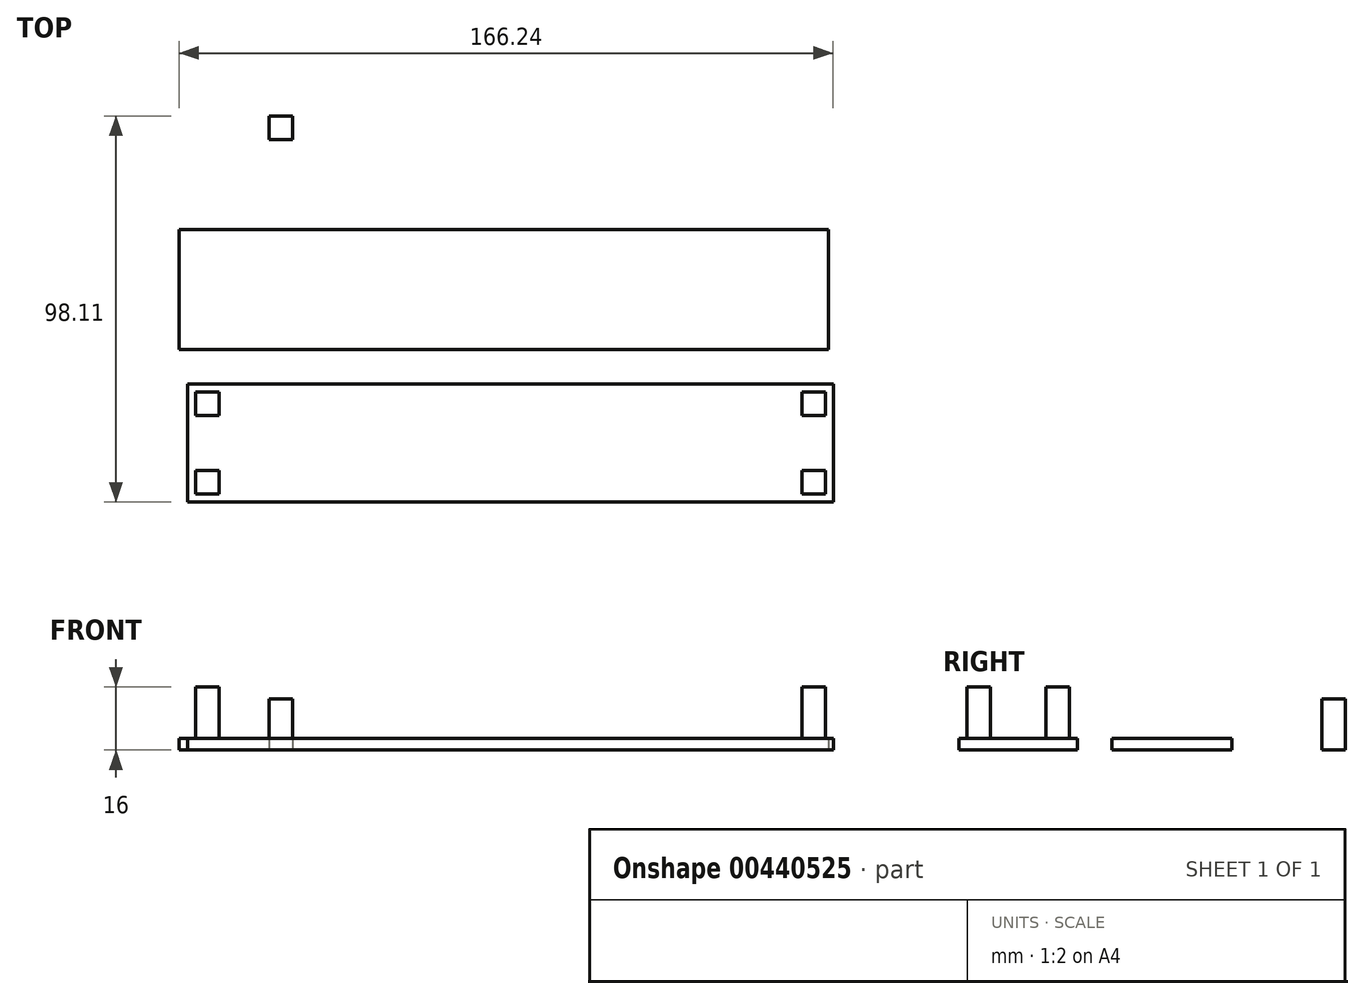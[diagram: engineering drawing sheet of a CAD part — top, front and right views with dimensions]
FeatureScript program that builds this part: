
annotation { "Feature Type Name" : "Feature", "Feature Type Description" : "" }
export const myFeature = defineFeature(function(context is Context, id is Id, definition is map)
    precondition{}
    {
        {
            var Q0;
            Q0=qCreatedBy(makeId("Top.planeOp"),FACE);
            var sketch = newSketch(context, id + "F0", { "sketchPlane" : qUnion([Q0])});
            skLineSegment(sketch, "E0.bottom", {"start": v(-85.08, 12.28) * mm, "end": v(79.92, 12.28) * mm});
            skLineSegment(sketch, "E0.top", {"start": v(-85.08, -18.22) * mm, "end": v(79.92, -18.22) * mm});
            skLineSegment(sketch, "E0.left", {"start": v(-85.08, 12.28) * mm, "end": v(-85.08, -18.22) * mm});
            skLineSegment(sketch, "E0.right", {"start": v(79.92, 12.28) * mm, "end": v(79.92, -18.22) * mm});
            skSolve(sketch);
        }
        {
            var Q0;
            Q0=qCreatedBy(makeId("Top.planeOp"),FACE);
            var sketch = newSketch(context, id + "F1", { "sketchPlane" : qUnion([Q0])});
            skLineSegment(sketch, "E1.bottom", {"start": v(-62.2, 41.13) * mm, "end": v(-56.2, 41.13) * mm});
            skLineSegment(sketch, "E1.top", {"start": v(-62.2, 35.13) * mm, "end": v(-56.2, 35.13) * mm});
            skLineSegment(sketch, "E1.left", {"start": v(-62.2, 41.13) * mm, "end": v(-62.2, 35.13) * mm});
            skLineSegment(sketch, "E1.right", {"start": v(-56.2, 41.13) * mm, "end": v(-56.2, 35.13) * mm});
            skSolve(sketch);
        }
        {
            var Q0;
            Q0=makeQuery(id+"F0.imprint","IMPRINT",FACE,{"disambiguationData":[TD([[makeQuery(id+"F0.imprint","IMPRINT",EDGE,{"derivedFrom":sQuery(id+"F0.wireOp",EDGE,"E0.bottom")}),-1.0]])]});
            extrude(context, id + "F2", {"entities" : qUnion([Q0]), "depth" : 3 * mm, "offsetDistance" : 25 * mm});
        }
        {
            var Q0;
            Q0=makeQuery(id+"F1.imprint","IMPRINT",FACE,{"disambiguationData":[TD([[makeQuery(id+"F1.imprint","IMPRINT",EDGE,{"derivedFrom":sQuery(id+"F1.wireOp",EDGE,"E1.bottom")}),-1.0]])]});
            extrude(context, id + "F3", {"entities" : qUnion([Q0]), "depth" : 13 * mm, "offsetDistance" : 25 * mm});
        }
        {
            var Q0;
            Q0=qCreatedBy(makeId("Top.planeOp"),FACE);
            var sketch = newSketch(context, id + "F4", { "sketchPlane" : qUnion([Q0])});
            skLineSegment(sketch, "E2.bottom", {"start": v(-82.84, -26.98) * mm, "end": v(81.16, -26.98) * mm});
            skLineSegment(sketch, "E2.top", {"start": v(-82.84, -56.98) * mm, "end": v(81.16, -56.98) * mm});
            skLineSegment(sketch, "E2.left", {"start": v(-82.84, -26.98) * mm, "end": v(-82.84, -56.98) * mm});
            skLineSegment(sketch, "E2.right", {"start": v(81.16, -26.98) * mm, "end": v(81.16, -56.98) * mm});
            skLineSegment(sketch, "E3.bottom", {"start": v(-80.84, -48.98) * mm, "end": v(-74.84, -48.98) * mm});
            skLineSegment(sketch, "E3.top", {"start": v(-80.84, -54.98) * mm, "end": v(-74.84, -54.98) * mm});
            skLineSegment(sketch, "E3.left", {"start": v(-80.84, -48.98) * mm, "end": v(-80.84, -54.98) * mm});
            skLineSegment(sketch, "E3.right", {"start": v(-74.84, -48.98) * mm, "end": v(-74.84, -54.98) * mm});
            skLineSegment(sketch, "E4.bottom", {"start": v(-80.84, -28.98) * mm, "end": v(-74.84, -28.98) * mm});
            skLineSegment(sketch, "E4.top", {"start": v(-80.84, -34.98) * mm, "end": v(-74.84, -34.98) * mm});
            skLineSegment(sketch, "E4.left", {"start": v(-80.84, -28.98) * mm, "end": v(-80.84, -34.98) * mm});
            skLineSegment(sketch, "E4.right", {"start": v(-74.84, -28.98) * mm, "end": v(-74.84, -34.98) * mm});
            skLineSegment(sketch, "E5.bottom", {"start": v(73.16, -28.98) * mm, "end": v(79.16, -28.98) * mm});
            skLineSegment(sketch, "E5.top", {"start": v(73.16, -34.98) * mm, "end": v(79.16, -34.98) * mm});
            skLineSegment(sketch, "E5.left", {"start": v(73.16, -28.98) * mm, "end": v(73.16, -34.98) * mm});
            skLineSegment(sketch, "E5.right", {"start": v(79.16, -28.98) * mm, "end": v(79.16, -34.98) * mm});
            skLineSegment(sketch, "E6.bottom", {"start": v(73.16, -48.98) * mm, "end": v(79.16, -48.98) * mm});
            skLineSegment(sketch, "E6.top", {"start": v(73.16, -54.98) * mm, "end": v(79.16, -54.98) * mm});
            skLineSegment(sketch, "E6.left", {"start": v(73.16, -48.98) * mm, "end": v(73.16, -54.98) * mm});
            skLineSegment(sketch, "E6.right", {"start": v(79.16, -48.98) * mm, "end": v(79.16, -54.98) * mm});
            skSolve(sketch);
        }
        {
            var Q0;
            Q0=makeQuery(id+"F4.imprint","IMPRINT",FACE,{"disambiguationData":[TD([[makeQuery(id+"F4.imprint","IMPRINT",EDGE,{"derivedFrom":sQuery(id+"F4.wireOp",EDGE,"E2.bottom")}),-1.0]])]});
            extrude(context, id + "F5", {"entities" : qUnion([Q0]), "depth" : 3 * mm, "offsetDistance" : 25 * mm});
        }
        {
            var Q0;
            Q0=makeQuery(id+"F4.imprint","IMPRINT",FACE,{"disambiguationData":[TD([[makeQuery(id+"F4.imprint","IMPRINT",EDGE,{"derivedFrom":sQuery(id+"F4.wireOp",EDGE,"E4.bottom")}),-1.0]])]});
            var Q1;
            Q1=makeQuery(id+"F4.imprint","IMPRINT",FACE,{"disambiguationData":[TD([[makeQuery(id+"F4.imprint","IMPRINT",EDGE,{"derivedFrom":sQuery(id+"F4.wireOp",EDGE,"E3.bottom")}),-1.0]])]});
            var Q2;
            Q2=makeQuery(id+"F4.imprint","IMPRINT",FACE,{"disambiguationData":[TD([[makeQuery(id+"F4.imprint","IMPRINT",EDGE,{"derivedFrom":sQuery(id+"F4.wireOp",EDGE,"E5.bottom")}),-1.0]])]});
            var Q3;
            Q3=makeQuery(id+"F4.imprint","IMPRINT",FACE,{"disambiguationData":[TD([[makeQuery(id+"F4.imprint","IMPRINT",EDGE,{"derivedFrom":sQuery(id+"F4.wireOp",EDGE,"E6.bottom")}),-1.0]])]});
            extrude(context, id + "F6", {"entities" : qUnion([Q0, Q1, Q2, Q3]), "operationType" : NewBodyOperationType.ADD, "depth" : 16 * mm, "offsetDistance" : 25 * mm});
        }
    });
